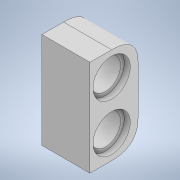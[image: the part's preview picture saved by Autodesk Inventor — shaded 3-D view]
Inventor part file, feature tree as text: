
AUTODESK INVENTOR PART (.ipt)
format: ipt  version: 2020 (Build 240168000, 168)  size: 321,024 bytes
history: native  units: mm
features: other x12, extrude x4, sketch x4
ambient origin geometry x8: Origin, YZ Plane, XZ Plane, XY Plane, X Axis, Y Axis, Z Axis, Center Point
bodies: Body1 (feature_tree)
feature tree (20):
  other  "Sólido1"
  extrude  "Extrusão1"  Depth=16.0mm
  extrude  "Extrusão3"  Depth=8.0mm TaperAngle=0.0deg
  extrude  "Extrusão4"  Depth=1.0mm TaperAngle=0.0deg
  extrude  "Extrusão5"  Depth=5.0mm
  sketch  "Esboço1"  dims[d0=8.0mm d1=16.0mm]
  sketch  "Esboço3"  dims[d2=8.0mm d3=0.0mm d8=8.0mm d9=0.0mm]
  other  "Referência3"
  other  "Referência4"
  sketch  "Esboço4"  dims[d10=1.0mm d11=0.0mm d12=1.0mm d13=0.0mm]
  other  "Referência5"
  other  "Referência6"
  sketch  "Esboço5"  dims[d14=5.0mm d15=5.0mm]
  other  "Referência7"
  other  "Referência8"
  other  "<userpath>\Desktop\rabo\3d\ela.iam"
  other  "ela.iam"
  other  "basesinha:1"
  other  "Component2_6_MIR:2"
  other  "Component2_6:3"
